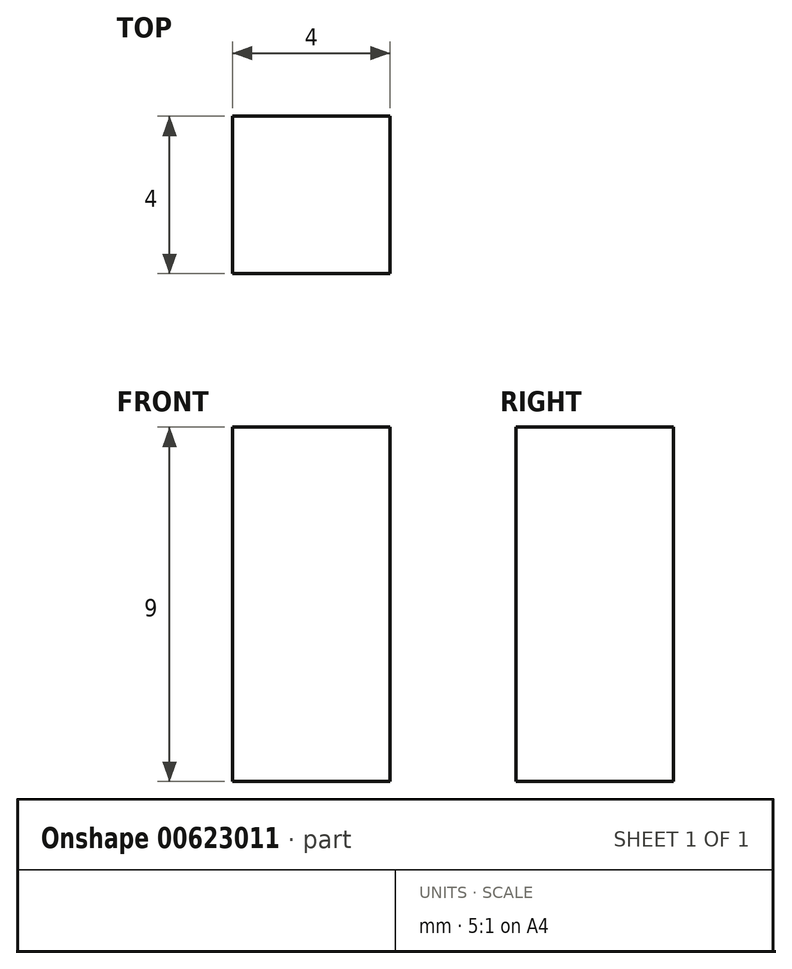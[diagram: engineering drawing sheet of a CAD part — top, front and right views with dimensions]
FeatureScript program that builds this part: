
annotation { "Feature Type Name" : "Feature", "Feature Type Description" : "" }
export const myFeature = defineFeature(function(context is Context, id is Id, definition is map)
    precondition{}
    {
        {
            var Q0;
            Q0=qCreatedBy(makeId("Right.planeOp"),FACE);
            var sketch = newSketch(context, id + "F0", { "sketchPlane" : qUnion([Q0])});
            skLineSegment(sketch, "E0.bottom", {"start": v(0, 0) * mm, "end": v(-100, 0) * mm});
            skLineSegment(sketch, "E0.top", {"start": v(0, 50) * mm, "end": v(-100, 50) * mm});
            skLineSegment(sketch, "E0.left", {"start": v(0, 0) * mm, "end": v(0, 50) * mm});
            skLineSegment(sketch, "E0.right", {"start": v(-100, 0) * mm, "end": v(-100, 50) * mm});
            skLineSegment(sketch, "E1.bottom", {"start": v(-25, 50) * mm, "end": v(-75, 50) * mm});
            skLineSegment(sketch, "E1.top", {"start": v(-25, 35) * mm, "end": v(-75, 35) * mm});
            skLineSegment(sketch, "E1.left", {"start": v(-25, 50) * mm, "end": v(-25, 35) * mm});
            skLineSegment(sketch, "E1.right", {"start": v(-75, 50) * mm, "end": v(-75, 35) * mm});
            skLineSegment(sketch, "E2.bottom", {"start": v(-100, 0) * mm, "end": v(-80, 0) * mm});
            skLineSegment(sketch, "E2.top", {"start": v(-100, 4) * mm, "end": v(-80, 4) * mm});
            skLineSegment(sketch, "E2.left", {"start": v(-100, 0) * mm, "end": v(-100, 4) * mm});
            skLineSegment(sketch, "E2.right", {"start": v(-80, 0) * mm, "end": v(-80, 4) * mm});
            skLineSegment(sketch, "E3.bottom", {"start": v(0, 0) * mm, "end": v(-20, 0) * mm});
            skLineSegment(sketch, "E3.top", {"start": v(0, 4) * mm, "end": v(-20, 4) * mm});
            skLineSegment(sketch, "E3.left", {"start": v(0, 0) * mm, "end": v(0, 4) * mm});
            skLineSegment(sketch, "E3.right", {"start": v(-20, 0) * mm, "end": v(-20, 4) * mm});
            skLineSegment(sketch, "E4.bottom", {"start": v(-40, 0) * mm, "end": v(-60, 0) * mm});
            skLineSegment(sketch, "E4.top", {"start": v(-40, 4) * mm, "end": v(-60, 4) * mm});
            skLineSegment(sketch, "E4.left", {"start": v(-40, 0) * mm, "end": v(-40, 4) * mm});
            skLineSegment(sketch, "E4.right", {"start": v(-60, 0) * mm, "end": v(-60, 4) * mm});
            skLineSegment(sketch, "E5.bottom", {"start": v(-100, 18) * mm, "end": v(-96, 18) * mm});
            skLineSegment(sketch, "E5.top", {"start": v(-100, 32) * mm, "end": v(-96, 32) * mm});
            skLineSegment(sketch, "E5.left", {"start": v(-100, 18) * mm, "end": v(-100, 32) * mm});
            skLineSegment(sketch, "E5.right", {"start": v(-96, 18) * mm, "end": v(-96, 32) * mm});
            skLineSegment(sketch, "E6.bottom", {"start": v(0, 32) * mm, "end": v(-4, 32) * mm});
            skLineSegment(sketch, "E6.top", {"start": v(0, 18) * mm, "end": v(-4, 18) * mm});
            skLineSegment(sketch, "E6.left", {"start": v(0, 32) * mm, "end": v(0, 18) * mm});
            skLineSegment(sketch, "E6.right", {"start": v(-4, 32) * mm, "end": v(-4, 18) * mm});
            skLineSegment(sketch, "E7.bottom", {"start": v(-59, 35) * mm, "end": v(-42, 35) * mm});
            skLineSegment(sketch, "E7.top", {"start": v(-59, 31) * mm, "end": v(-42, 31) * mm});
            skLineSegment(sketch, "E7.left", {"start": v(-59, 35) * mm, "end": v(-59, 31) * mm});
            skLineSegment(sketch, "E7.right", {"start": v(-42, 35) * mm, "end": v(-42, 31) * mm});
            skLineSegment(sketch, "E8.bottom", {"start": v(-25, 43) * mm, "end": v(-21, 43) * mm});
            skLineSegment(sketch, "E8.top", {"start": v(-25, 34) * mm, "end": v(-21, 34) * mm});
            skLineSegment(sketch, "E8.left", {"start": v(-25, 43) * mm, "end": v(-25, 34) * mm});
            skLineSegment(sketch, "E8.right", {"start": v(-21, 43) * mm, "end": v(-21, 34) * mm});
            skLineSegment(sketch, "E9.bottom", {"start": v(-75, 43) * mm, "end": v(-79, 43) * mm});
            skLineSegment(sketch, "E9.top", {"start": v(-75, 34) * mm, "end": v(-79, 34) * mm});
            skLineSegment(sketch, "E9.left", {"start": v(-75, 43) * mm, "end": v(-75, 34) * mm});
            skLineSegment(sketch, "E9.right", {"start": v(-79, 43) * mm, "end": v(-79, 34) * mm});
            skSolve(sketch);
        }
        {
            var Q0;
            {var subQ5=sQuery(id+"F0.wireOp",EDGE,"E1.left");Q0=makeQuery(id+"F0.imprint","IMPRINT",FACE,{"disambiguationData":[TD([[makeQuery(id+"F0.imprint","IMPRINT",EDGE,{"derivedFrom":subQ5}),1.0]])]});}
            extrude(context, id + "F1", {"entities" : qUnion([Q0]), "depth" : 4 * mm, "offsetDistance" : 25 * mm});
        }
        {
            var Q0;
            Q0=qCreatedBy(makeId("Right.planeOp"),FACE);
            var sketch = newSketch(context, id + "F2", { "sketchPlane" : qUnion([Q0])});
            skLineSegment(sketch, "E10.bottom", {"start": v(-94, 50) * mm, "end": v(-81.5, 50) * mm});
            skLineSegment(sketch, "E10.top", {"start": v(-94, 46) * mm, "end": v(-81.5, 46) * mm});
            skLineSegment(sketch, "E10.left", {"start": v(-94, 50) * mm, "end": v(-94, 46) * mm});
            skLineSegment(sketch, "E10.right", {"start": v(-81.5, 50) * mm, "end": v(-81.5, 46) * mm});
            skLineSegment(sketch, "E11.bottom", {"start": v(-18.5, 50.12) * mm, "end": v(-6, 50.12) * mm});
            skLineSegment(sketch, "E11.top", {"start": v(-18.5, 46.12) * mm, "end": v(-6, 46.12) * mm});
            skLineSegment(sketch, "E11.left", {"start": v(-18.5, 50.12) * mm, "end": v(-18.5, 46.12) * mm});
            skLineSegment(sketch, "E11.right", {"start": v(-6, 50.12) * mm, "end": v(-6, 46.12) * mm});
            skSolve(sketch);
        }
        {
            var Q0;
            Q0 = qSketchRegion(id + "F2", true);
            extrude(context, id + "F3", {"entities" : qUnion([Q0]), "operationType" : NewBodyOperationType.REMOVE, "depth" : 4 * mm, "offsetDistance" : 25 * mm});
        }
    });
